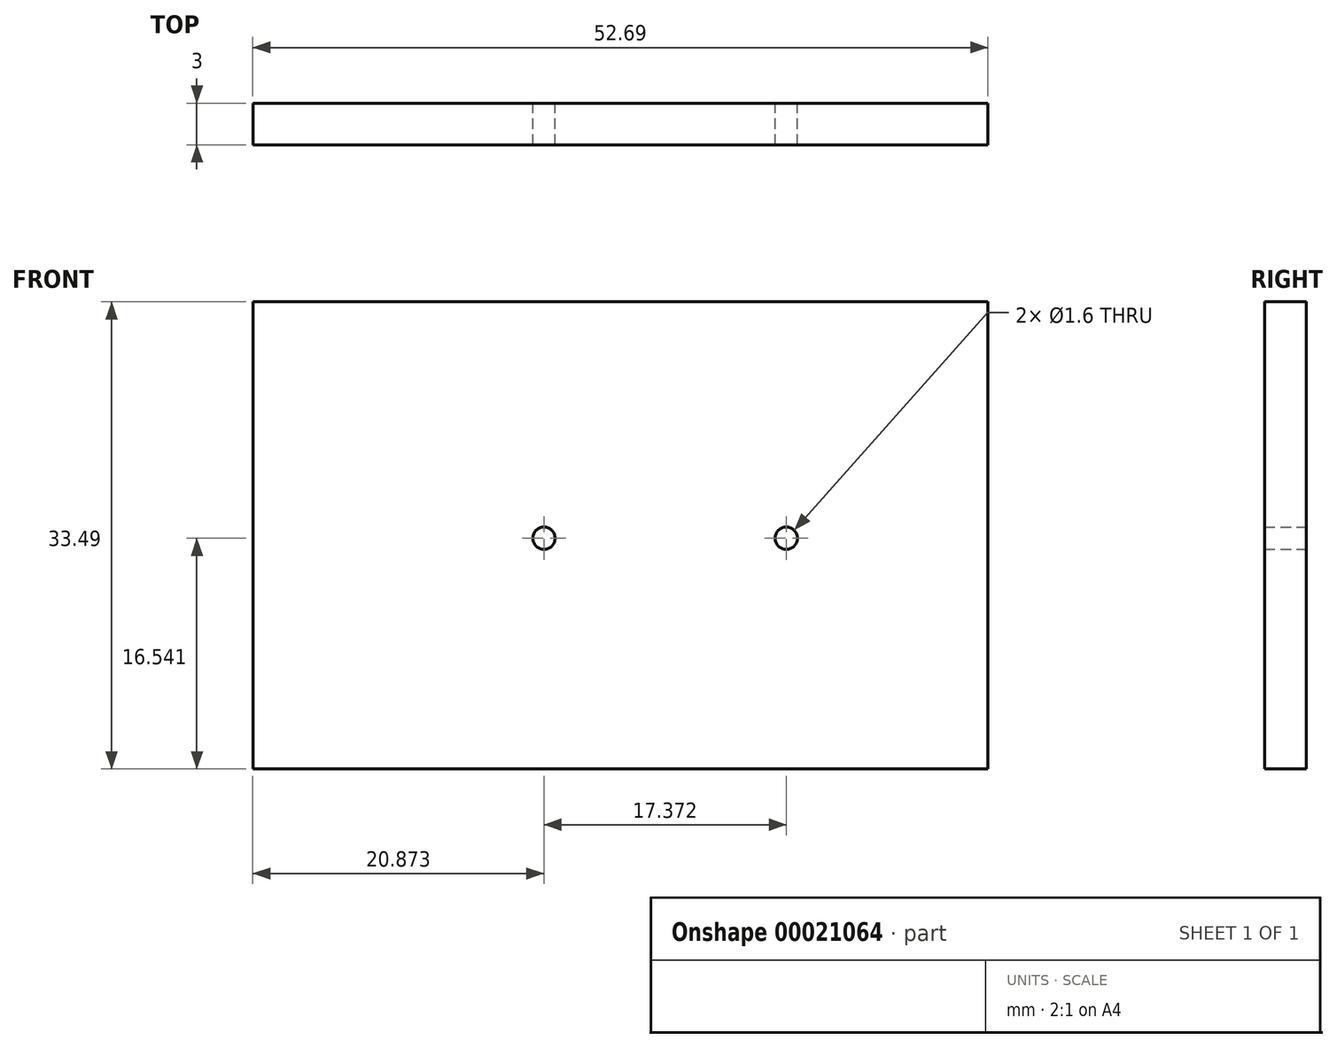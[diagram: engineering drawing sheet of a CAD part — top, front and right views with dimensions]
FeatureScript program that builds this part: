
annotation { "Feature Type Name" : "Feature", "Feature Type Description" : "" }
export const myFeature = defineFeature(function(context is Context, id is Id, definition is map)
    precondition{}
    {
        {
            var Q0;
            Q0=qCreatedBy(makeId("Front.planeOp"),FACE);
            var sketch = newSketch(context, id + "F0", { "sketchPlane" : qUnion([Q0])});
            skCircle(sketch, "E0", {"center": v(9.05, 13.25) * mm, "radius": 0.8 * mm});
            skCircle(sketch, "E1", {"center": v(26.42, 13.25) * mm, "radius": 0.8 * mm});
            skLineSegment(sketch, "E2.bottom", {"start": v(-11.82, 30.2) * mm, "end": v(40.87, 30.2) * mm});
            skLineSegment(sketch, "E2.top", {"start": v(-11.82, -3.3) * mm, "end": v(40.87, -3.3) * mm});
            skLineSegment(sketch, "E2.left", {"start": v(-11.82, 30.2) * mm, "end": v(-11.82, -3.3) * mm});
            skLineSegment(sketch, "E2.right", {"start": v(40.87, 30.2) * mm, "end": v(40.87, -3.3) * mm});
            skSolve(sketch);
        }
        {
            var Q0;
            Q0 = qSketchRegion(id + "F0", true);
            extrude(context, id + "F1", {"entities" : qUnion([Q0]), "depth" : 3 * mm});
        }
    });
